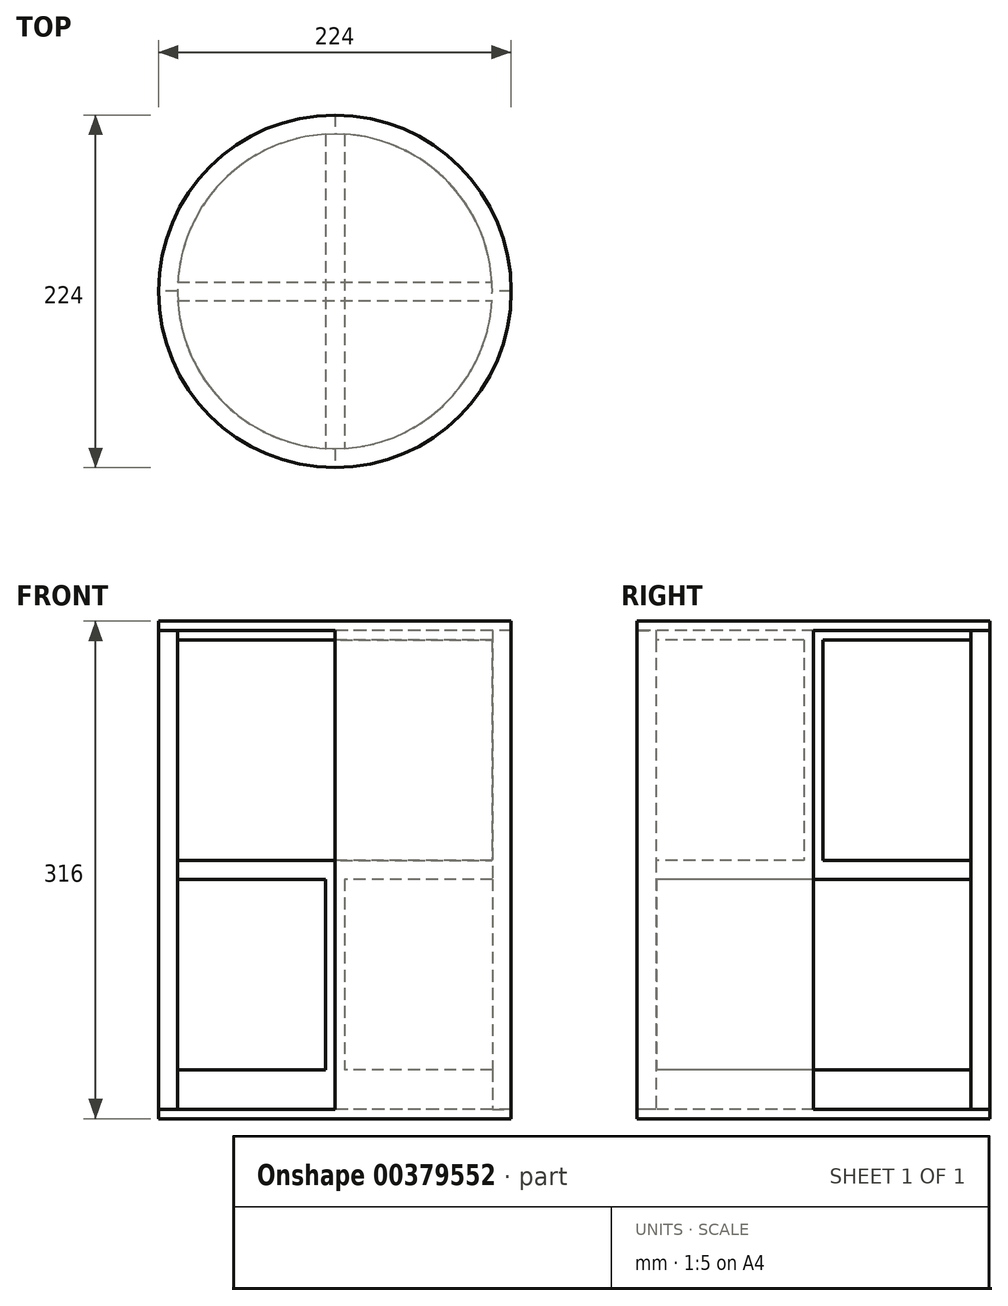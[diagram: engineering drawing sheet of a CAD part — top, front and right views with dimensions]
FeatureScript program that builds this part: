
annotation { "Feature Type Name" : "Feature", "Feature Type Description" : "" }
export const myFeature = defineFeature(function(context is Context, id is Id, definition is map)
    precondition{}
    {
        {
            var Q0;
            Q0=qCreatedBy(makeId("Top.planeOp"),FACE);
            var sketch = newSketch(context, id + "F0", { "sketchPlane" : qUnion([Q0])});
            skCircle(sketch, "E0", {"center": v(0, 0) * mm, "radius": 112 * mm});
            skSolve(sketch);
        }
        {
            var Q0;
            Q0=makeQuery(id+"F0.imprint","IMPRINT",FACE,{"disambiguationData":[TD([[makeQuery(id+"F0.imprint","IMPRINT",EDGE,{"derivedFrom":sQuery(id+"F0.wireOp",EDGE,"E0")}),1.0]])]});
            extrude(context, id + "F1", {"entities" : qUnion([Q0]), "depth" : 6 * mm});
        }
        {
            var Q0;
            Q0=makeQuery(id+"F1.opExtrude","CAP_FACE",FACE,{"disambiguationData":[OSD([sQuery(id+"F0.wireOp",EDGE,"E0")])],"isStart":false});
            var sketch = newSketch(context, id + "F2", { "sketchPlane" : qUnion([Q0])});
            skCircle(sketch, "E1", {"center": v(0, 0) * mm, "radius": 100 * mm});
            skLineSegment(sketch, "E2", {"start": v(-100, 0) * mm, "end": v(-118, 0) * mm});
            skLineSegment(sketch, "E3", {"start": v(0, 100) * mm, "end": v(0, 112) * mm});
            skSolve(sketch);
        }
        {
            var Q0;
            Q0=makeQuery(id+"F2.imprint","IMPRINT",FACE,{"disambiguationData":[TD([[makeQuery(id+"F2.imprint","IMPRINT",EDGE,{"derivedFrom":sQuery(id+"F2.wireOp",EDGE,"E1")}),1.0]])]});
            extrude(context, id + "F3", {"entities" : qUnion([Q0]), "operationType" : NewBodyOperationType.ADD, "depth" : 6 * mm});
        }
        {
            var Q0;
            Q0=makeQuery(id+"F3.opExtrude","CAP_FACE",FACE,{"disambiguationData":[OSD([sQuery(id+"F2.wireOp",EDGE,"E1")])],"isStart":false});
            var sketch = newSketch(context, id + "F4", { "sketchPlane" : qUnion([Q0])});
            skLineSegment(sketch, "E4.bottom", {"start": v(6, 100) * mm, "end": v(-6, 100) * mm});
            skLineSegment(sketch, "E4.top", {"start": v(6, -100) * mm, "end": v(-6, -100) * mm});
            skLineSegment(sketch, "E4.left", {"start": v(6, 100) * mm, "end": v(6, -100) * mm});
            skLineSegment(sketch, "E4.right", {"start": v(-6, 100) * mm, "end": v(-6, -100) * mm});
            skPoint(sketch, "E4.middle", {"position": v(0, 0) * mm});
            skSolve(sketch);
        }
        {
            var Q0;
            {var subQ0=makeQuery(id+"F3.opExtrude","CAP_EDGE",EDGE,{"disambiguationData":[OSD([sQuery(id+"F2.wireOp",EDGE,"E1")])],"isStart":false});var subQ2=sQuery(id+"F4.wireOp",EDGE,"E4.left");var subQ3=makeQuery(id+"F4.imprint","INTERSECT",VERTEX,{"disambiguationData":[OD(0.0)],"derivedFrom":[subQ0,subQ2]});Q0=makeQuery(id+"F4.imprint","IMPRINT",FACE,{"disambiguationData":[TD([[makeQuery(id+"F4.imprint","IMPRINT",EDGE,{"disambiguationData":[TD([[subQ3,-1.0]])],"derivedFrom":subQ2}),-1.0]])]});}
            extrude(context, id + "F5", {"entities" : qUnion([Q0]), "operationType" : NewBodyOperationType.ADD, "depth" : 140 * mm});
        }
        {
            var Q0;
            Q0=makeQuery(id+"F5.opExtrude","CAP_FACE",FACE,{"disambiguationData":[OSD([sQuery(id+"F2.wireOp",EDGE,"E1"),sQuery(id+"F4.wireOp",EDGE,"E4.left"),sQuery(id+"F4.wireOp",EDGE,"E4.right")])],"isStart":false});
            var sketch = newSketch(context, id + "F6", { "sketchPlane" : qUnion([Q0])});
            skCircle(sketch, "E5", {"center": v(0, 0) * mm, "radius": 100 * mm});
            skSolve(sketch);
        }
        {
            var Q0;
            {var subQ1=makeQuery(id+"F5.opExtrude","CAP_EDGE",EDGE,{"disambiguationData":[OSD([sQuery(id+"F4.wireOp",EDGE,"E4.right")])],"isStart":false});Q0=makeQuery(id+"F6.imprint","IMPRINT",FACE,{"disambiguationData":[TD([[makeQuery(id+"F6.imprint","IMPRINT",EDGE,{"derivedFrom":subQ1}),-1.0]])]});}
            var Q1;
            {var subQ1=makeQuery(id+"F5.opExtrude","CAP_EDGE",EDGE,{"disambiguationData":[OSD([sQuery(id+"F4.wireOp",EDGE,"E4.left")])],"isStart":false});Q1=makeQuery(id+"F6.imprint","IMPRINT",FACE,{"disambiguationData":[TD([[makeQuery(id+"F6.imprint","IMPRINT",EDGE,{"derivedFrom":subQ1}),-1.0]])]});}
            var Q2;
            {var subQ1=makeQuery(id+"F5.opExtrude","CAP_EDGE",EDGE,{"disambiguationData":[OSD([sQuery(id+"F4.wireOp",EDGE,"E4.left")])],"isStart":false});Q2=makeQuery(id+"F6.imprint","IMPRINT",FACE,{"disambiguationData":[TD([[makeQuery(id+"F6.imprint","IMPRINT",EDGE,{"derivedFrom":subQ1}),1.0]])]});}
            extrude(context, id + "F7", {"entities" : qUnion([Q0, Q1, Q2]), "operationType" : NewBodyOperationType.ADD, "depth" : 12 * mm});
        }
        {
            var Q0;
            Q0=makeQuery(id+"F7.opExtrude","CAP_FACE",FACE,{"disambiguationData":[OSD([sQuery(id+"F6.wireOp",EDGE,"E5")])],"isStart":false});
            var sketch = newSketch(context, id + "F8", { "sketchPlane" : qUnion([Q0])});
            skLineSegment(sketch, "E6.bottom", {"start": v(-100, 6) * mm, "end": v(100, 6) * mm});
            skLineSegment(sketch, "E6.top", {"start": v(-100, -6) * mm, "end": v(100, -6) * mm});
            skLineSegment(sketch, "E6.left", {"start": v(-100, 6) * mm, "end": v(-100, -6) * mm});
            skLineSegment(sketch, "E6.right", {"start": v(100, 6) * mm, "end": v(100, -6) * mm});
            skPoint(sketch, "E6.middle", {"position": v(0, 0) * mm});
            skSolve(sketch);
        }
        {
            var Q0;
            {var subQ0=sQuery(id+"F8.wireOp",EDGE,"E6.bottom");var subQ1=makeQuery(id+"F7.opExtrude","CAP_EDGE",EDGE,{"disambiguationData":[OSD([sQuery(id+"F6.wireOp",EDGE,"E5")])],"isStart":false});var subQ4=makeQuery(id+"F8.imprint","INTERSECT",VERTEX,{"disambiguationData":[OD(0.0)],"derivedFrom":[subQ1,subQ0]});Q0=makeQuery(id+"F8.imprint","IMPRINT",FACE,{"disambiguationData":[TD([[makeQuery(id+"F8.imprint","IMPRINT",EDGE,{"disambiguationData":[TD([[subQ4,-1.0]])],"derivedFrom":subQ0}),-1.0]])]});}
            extrude(context, id + "F9", {"entities" : qUnion([Q0]), "operationType" : NewBodyOperationType.ADD, "depth" : 140 * mm});
        }
        {
            var Q0;
            Q0=makeQuery(id+"F9.opExtrude","CAP_FACE",FACE,{"disambiguationData":[OSD([sQuery(id+"F6.wireOp",EDGE,"E5"),sQuery(id+"F8.wireOp",EDGE,"E6.bottom"),sQuery(id+"F8.wireOp",EDGE,"E6.top")])],"isStart":false});
            var sketch = newSketch(context, id + "F10", { "sketchPlane" : qUnion([Q0])});
            skCircle(sketch, "E7", {"center": v(0, 0) * mm, "radius": 100 * mm});
            skSolve(sketch);
        }
        {
            var Q0;
            {var subQ1=makeQuery(id+"F9.opExtrude","CAP_EDGE",EDGE,{"disambiguationData":[OSD([sQuery(id+"F8.wireOp",EDGE,"E6.bottom")])],"isStart":false});Q0=makeQuery(id+"F10.imprint","IMPRINT",FACE,{"disambiguationData":[TD([[makeQuery(id+"F10.imprint","IMPRINT",EDGE,{"derivedFrom":subQ1}),1.0]])]});}
            var Q1;
            {var subQ1=makeQuery(id+"F9.opExtrude","CAP_EDGE",EDGE,{"disambiguationData":[OSD([sQuery(id+"F8.wireOp",EDGE,"E6.bottom")])],"isStart":false});Q1=makeQuery(id+"F10.imprint","IMPRINT",FACE,{"disambiguationData":[TD([[makeQuery(id+"F10.imprint","IMPRINT",EDGE,{"derivedFrom":subQ1}),-1.0]])]});}
            var Q2;
            {var subQ1=makeQuery(id+"F9.opExtrude","CAP_EDGE",EDGE,{"disambiguationData":[OSD([sQuery(id+"F8.wireOp",EDGE,"E6.top")])],"isStart":false});Q2=makeQuery(id+"F10.imprint","IMPRINT",FACE,{"disambiguationData":[TD([[makeQuery(id+"F10.imprint","IMPRINT",EDGE,{"derivedFrom":subQ1}),-1.0]])]});}
            extrude(context, id + "F11", {"entities" : qUnion([Q0, Q1, Q2]), "operationType" : NewBodyOperationType.ADD, "depth" : 6 * mm});
        }
        {
            var Q0;
            Q0=makeQuery(id+"F11.opExtrude","CAP_FACE",FACE,{"disambiguationData":[OSD([sQuery(id+"F10.wireOp",EDGE,"E7")])],"isStart":false});
            var sketch = newSketch(context, id + "F12", { "sketchPlane" : qUnion([Q0])});
            skCircle(sketch, "E8", {"center": v(0, 0) * mm, "radius": 112 * mm});
            skSolve(sketch);
        }
        {
            var Q0;
            Q0=makeQuery(id+"F12.imprint","IMPRINT",FACE,{"disambiguationData":[TD([[makeQuery(id+"F12.imprint","IMPRINT",EDGE,{"derivedFrom":sQuery(id+"F12.wireOp",EDGE,"E8")}),1.0]])]});
            var Q1;
            Q1=makeQuery(id+"F12.imprint","IMPRINT",FACE,{"disambiguationData":[TD([[makeQuery(id+"F12.imprint","IMPRINT",EDGE,{"derivedFrom":makeQuery(id+"F11.opExtrude","CAP_EDGE",EDGE,{"disambiguationData":[OSD([sQuery(id+"F10.wireOp",EDGE,"E7")])],"isStart":false})}),1.0]])]});
            extrude(context, id + "F13", {"entities" : qUnion([Q0, Q1]), "operationType" : NewBodyOperationType.ADD, "depth" : 6 * mm});
        }
        {
            var Q0;
            Q0 = qSketchRegion(id + "F2", true);
            extrude(context, id + "F14", {"entities" : qUnion([Q0]), "operationType" : NewBodyOperationType.ADD, "depth" : 25 * mm});
        }
        {
            var Q0;
            Q0=makeQuery(id+"F1.opExtrude","CAP_FACE",FACE,{"disambiguationData":[OSD([sQuery(id+"F0.wireOp",EDGE,"E0")])],"isStart":false});
            var sketch = newSketch(context, id + "F15", { "sketchPlane" : qUnion([Q0])});
            skCircle(sketch, "E9", {"center": v(0, 0) * mm, "radius": 112 * mm});
            skCircle(sketch, "E10", {"center": v(0, 0) * mm, "radius": 100 * mm});
            skLineSegment(sketch, "E11", {"start": v(0, 0) * mm, "end": v(-115.65, 0) * mm});
            skLineSegment(sketch, "E12", {"start": v(0, 0) * mm, "end": v(0, 115.98) * mm});
            skLineSegment(sketch, "E13", {"start": v(0, 0) * mm, "end": v(119.22, 0) * mm});
            skLineSegment(sketch, "E14", {"start": v(0, 0) * mm, "end": v(0, -117.28) * mm});
            skSolve(sketch);
        }
        {
            var Q0;
            {var subQ0=sQuery(id+"F15.wireOp",EDGE,"E12");var subQ1=sQuery(id+"F15.wireOp",EDGE,"E9");var subQ2=makeQuery(id+"F15.imprint","INTERSECT",VERTEX,{"derivedFrom":[subQ1,subQ0]});Q0=makeQuery(id+"F15.imprint","IMPRINT",FACE,{"disambiguationData":[TD([[makeQuery(id+"F15.imprint","IMPRINT",EDGE,{"disambiguationData":[TD([[subQ2,-1.0]])],"derivedFrom":subQ1}),1.0]])]});}
            var Q1;
            {var subQ0=sQuery(id+"F15.wireOp",EDGE,"E13");var subQ1=sQuery(id+"F15.wireOp",EDGE,"E9");var subQ2=makeQuery(id+"F15.imprint","INTERSECT",VERTEX,{"derivedFrom":[subQ1,subQ0]});Q1=makeQuery(id+"F15.imprint","IMPRINT",FACE,{"disambiguationData":[TD([[makeQuery(id+"F15.imprint","IMPRINT",EDGE,{"disambiguationData":[TD([[subQ2,1.0]])],"derivedFrom":subQ1}),1.0]])]});}
            extrude(context, id + "F16", {"entities" : qUnion([Q0, Q1]), "operationType" : NewBodyOperationType.ADD, "depth" : 310 * mm});
        }
    });
